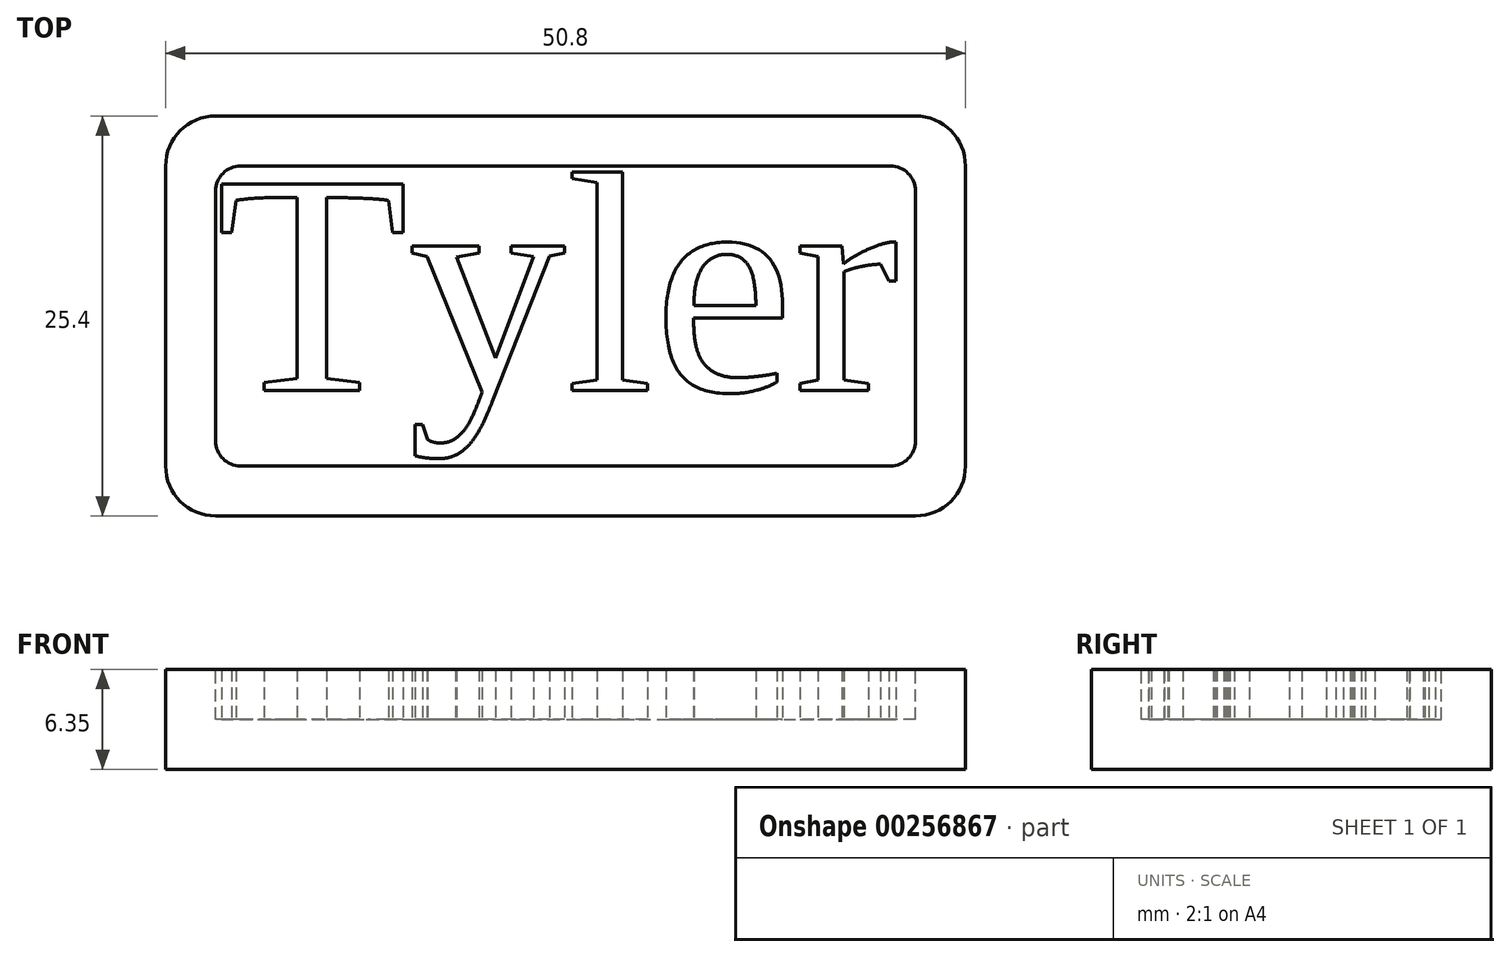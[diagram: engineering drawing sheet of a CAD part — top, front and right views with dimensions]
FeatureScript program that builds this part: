
annotation { "Feature Type Name" : "Feature", "Feature Type Description" : "" }
export const myFeature = defineFeature(function(context is Context, id is Id, definition is map)
    precondition{}
    {
        {
            var Q0;
            Q0=qCreatedBy(makeId("Top.planeOp"),FACE);
            var sketch = newSketch(context, id + "F0", { "sketchPlane" : qUnion([Q0])});
            skLineSegment(sketch, "E0", {"start": v(3.18, 25.4) * mm, "end": v(47.62, 25.4) * mm});
            skLineSegment(sketch, "E1", {"start": v(50.8, 22.23) * mm, "end": v(50.8, 3.18) * mm});
            skLineSegment(sketch, "E2", {"start": v(47.62, 0) * mm, "end": v(3.18, 0) * mm});
            skLineSegment(sketch, "E3", {"start": v(0, 3.18) * mm, "end": v(0, 22.23) * mm});
            skPoint(sketch, "E4.visualSharp", {"position": v(0, 25.4) * mm});
            skArc(sketch, "E4.filletArc", {"start": v(3.18, 25.4) * mm, "mid": v(0.93, 24.47) * mm, "end": v(0, 22.23) * mm});
            skPoint(sketch, "E5.visualSharp", {"position": v(50.8, 25.4) * mm});
            skArc(sketch, "E5.filletArc", {"start": v(50.8, 22.23) * mm, "mid": v(49.87, 24.47) * mm, "end": v(47.62, 25.4) * mm});
            skPoint(sketch, "E6.visualSharp", {"position": v(50.8, 0) * mm});
            skArc(sketch, "E6.filletArc", {"start": v(47.62, 0) * mm, "mid": v(49.87, 0.93) * mm, "end": v(50.8, 3.18) * mm});
            skPoint(sketch, "E7.visualSharp", {"position": v(0, 0) * mm});
            skArc(sketch, "E7.filletArc", {"start": v(0, 3.18) * mm, "mid": v(0.93, 0.93) * mm, "end": v(3.18, 0) * mm});
            skSolve(sketch);
        }
        {
            var Q0;
            Q0=makeQuery(id+"F0.imprint","IMPRINT",FACE,{"disambiguationData":[TD([[makeQuery(id+"F0.imprint","IMPRINT",EDGE,{"derivedFrom":sQuery(id+"F0.wireOp",EDGE,"E0")}),-1.0]])]});
            extrude(context, id + "F1", {"entities" : qUnion([Q0]), "depth" : 6.35 * mm});
        }
        {
            var Q0;
            Q0=makeQuery(id+"F1.opExtrude","CAP_FACE",FACE,{"disambiguationData":[OSD([sQuery(id+"F0.wireOp",EDGE,"E0"),sQuery(id+"F0.wireOp",EDGE,"E1"),sQuery(id+"F0.wireOp",EDGE,"E2"),sQuery(id+"F0.wireOp",EDGE,"E3"),sQuery(id+"F0.wireOp",EDGE,"E4.filletArc"),sQuery(id+"F0.wireOp",EDGE,"E5.filletArc"),sQuery(id+"F0.wireOp",EDGE,"E6.filletArc"),sQuery(id+"F0.wireOp",EDGE,"E7.filletArc")])],"isStart":false});
            var sketch = newSketch(context, id + "F2", { "sketchPlane" : qUnion([Q0])});
            skLineSegment(sketch, "E8", {"start": v(4.76, 22.23) * mm, "end": v(46.04, 22.22) * mm});
            skLineSegment(sketch, "E9", {"start": v(47.62, 20.64) * mm, "end": v(47.62, 4.76) * mm});
            skLineSegment(sketch, "E10", {"start": v(46.04, 3.18) * mm, "end": v(4.76, 3.18) * mm});
            skLineSegment(sketch, "E11", {"start": v(3.18, 4.76) * mm, "end": v(3.18, 20.64) * mm});
            skPoint(sketch, "E12.visualSharp", {"position": v(3.18, 22.23) * mm});
            skArc(sketch, "E12.filletArc", {"start": v(4.76, 22.23) * mm, "mid": v(3.64, 21.76) * mm, "end": v(3.17, 20.64) * mm});
            skPoint(sketch, "E13.visualSharp", {"position": v(47.62, 22.22) * mm});
            skArc(sketch, "E13.filletArc", {"start": v(47.62, 20.64) * mm, "mid": v(47.16, 21.76) * mm, "end": v(46.04, 22.22) * mm});
            skPoint(sketch, "E14.visualSharp", {"position": v(47.62, 3.18) * mm});
            skArc(sketch, "E14.filletArc", {"start": v(46.04, 3.18) * mm, "mid": v(47.16, 3.64) * mm, "end": v(47.62, 4.76) * mm});
            skPoint(sketch, "E15.visualSharp", {"position": v(3.18, 3.18) * mm});
            skArc(sketch, "E15.filletArc", {"start": v(3.17, 4.76) * mm, "mid": v(3.64, 3.64) * mm, "end": v(4.76, 3.18) * mm});
            skSolve(sketch);
        }
        {
            var Q0;
            Q0=makeQuery(id+"F2.imprint","IMPRINT",FACE,{"disambiguationData":[TD([[makeQuery(id+"F2.imprint","IMPRINT",EDGE,{"derivedFrom":sQuery(id+"F2.wireOp",EDGE,"E8")}),-1.0]])]});
            extrude(context, id + "F3", {"entities" : qUnion([Q0]), "operationType" : NewBodyOperationType.REMOVE, "oppositeDirection" : true, "depth" : 3.17 * mm});
        }
        {
            var Q0;
            Q0=makeQuery(id+"F3.boolean.opBoolean","COPY",FACE,{"derivedFrom":makeQuery(id+"F3.opExtrude","CAP_FACE",FACE,{"disambiguationData":[OSD([sQuery(id+"F2.wireOp",EDGE,"E8"),sQuery(id+"F2.wireOp",EDGE,"E9"),sQuery(id+"F2.wireOp",EDGE,"E10"),sQuery(id+"F2.wireOp",EDGE,"E11"),sQuery(id+"F2.wireOp",EDGE,"E12.filletArc"),sQuery(id+"F2.wireOp",EDGE,"E13.filletArc"),sQuery(id+"F2.wireOp",EDGE,"E14.filletArc"),sQuery(id+"F2.wireOp",EDGE,"E15.filletArc")])],"isStart":false})});
            var sketch = newSketch(context, id + "F4", { "sketchPlane" : qUnion([Q0])});
            skText(sketch, "E16", { "text": "Tyler", "fontName": "Tinos-Regular.ttf"});
            const initialGuessF4  = {"E16": [0.00318, 0.00796, 1, 0, 0.01442]};
            skSetInitialGuess(sketch, initialGuessF4);
            skSolve(sketch);
        }
        {
            var Q0;
            Q0 = qSketchRegion(id + "F4", true);
            extrude(context, id + "F5", {"entities" : qUnion([Q0]), "operationType" : NewBodyOperationType.ADD, "depth" : 3.17 * mm});
        }
    });
